# Revit family: io Wall 665
name_source: partatom
category: Lighting Fixtures
revit_build: Autodesk Revit 2018 (Build: 20170223_1515(x64)
units: mm (PartAtom-declared; Revit-internal decimal feet)

## family parameters
Always vertical = Yes
Cut with Voids When Loaded = No
Host = Wall
Light Source = Yes
OmniClass Number = 23.80.70.00
OmniClass Title = Lighting
Part Type = Normal
Room Calculation Point = No
Round Connector Dimension = Use Diameter
Shared = No

## types (1)
- CE
    Apparent Load = 8 VA
    Color Filter = 16777215
    Dimmable = Yes
    Dimming Lamp Color Temperature Shift = <None>
    Dimming Method = Phase - Trailing edge
    Driver Included = Yes
    Driver Required = No
    Efficacy (lm/w) = 101
    Electrical Class = 2
    Lamp = LED (integral)
    Light Source Fixed = Yes
    Location rating = IP44
    Main Finish = Clear Glass
    Main Material = Glass - Borosilicate
    Manufacturer = Astro Lighting Ltd
    Photometric Web File = GNC-23843 io 665 IES.ies
    Power (Watts) = 8.2
    Product Code = 1409002
    Product Location = Bathroom
    Product Name = io 665
    Product SKU = 1409002
    Tilt Angle = 0.00°
    URL = www.astrolighting.com

## geometry (parser evidence)
native form markers: Sweep x1
no freeform markers — native parametric forms only
